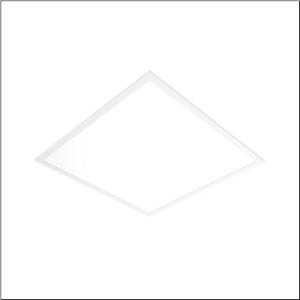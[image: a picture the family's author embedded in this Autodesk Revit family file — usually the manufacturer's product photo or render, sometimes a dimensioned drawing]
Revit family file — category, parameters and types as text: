
# Revit family: apollon_r__41_51mh12w72443_3f91
name_source: partatom
category: Lighting Fixtures
units: mm (PartAtom-declared; Revit-internal decimal feet)

## family parameters
Cut with Voids When Loaded = No
Host = Face
Light Source = No
Part Type = Normal
Room Calculation Point = No
Round Connector Dimension = Use Diameter
Shared = No

## types (1)
- Apollon® 41 (1 x LED, 3700 lm, 28.5 W, 4000K)
    Apparent Load = 29 VA
    CIE Flux Codes = 61 87 97 100 100
    Color Rendering = 80
    Color Temperature = 4000K
    Default Elevation = 1800 mm
    Description = Apollon® 41, office luminaire, primary optical cover: prismatic diffuser, of PS, light emission: direct distribution, primary light characteristic: symmetric, installation type: lay-in mounting, LED, rated luminous flux: 3.700lm, luminous efficacy: 130lm/W, light colour: 840, colour temperature: 4000K, with terminal, 3-pole, mains connection: 220..240V, AC, 50/60Hz, housing, of aluminium section, traffic white (RAL 9016), module: M600, length: 600mm, width: 600mm, height: 28mm, housing upper side, of sheet steel, protection rating (complete): IP20, protection rating (lamp compartment, on room side): IP40, insulation class (complete): insulation class II (safety insulation), certification: CE, ENEC, permissible operating ambient temperature: -25..+40°C, packaging unit: 1 piece
    Height = 0 mm  [stored 0 ft]
    Lamp = 1 x LED
    Lamp Light Flux = 3700 lm
    Lamp Power = 28.5 W
    Lamp count = 1
    Length = 600 mm
    Luminous efficacy = 130 lm/W
    Manufacturer = Siteco
    ModVariant = No
    Model = 51MH12W72443
    Mounting Place = Ceiling
    Mounting Type = Recessed
    Number of Poles = 1
    OnlyDefault = Yes
    Power Factor = 1
    Product Name = Apollon® 41
    Product group = office luminaire | ceiling recessed
    ProductGroupID = 400
    Protection Class = Protection class II
    Protection Degree = IP 20
    RLX_Detail_Level = 1
    RLX_Emergency_Light_Flux = 0 lm
    RLX_Emergency_Type = 0
    RLX_Emergency_Type_DB = No
    RlxData = <blob elided: 12189 chars, md5=490a4092>
    Socket = socket
    Standby Power = 0 W
    System Light Flux = 3700 lm
    System Power = 29 W
    Type Comments = Product without accessories
    Type Image = l_1291024.jpg
    URL = http://relux.com
    VarID = ---
    Voltage = 0 V
    Weight = 0.00 kg
    Width = 600 mm

note: [stored X ft] marks values corroborated as IEEE doubles in the binary element streams (Revit-internal decimal feet)

## geometry (parser evidence)
native form markers: Sweep x9
no freeform markers — native parametric forms only
